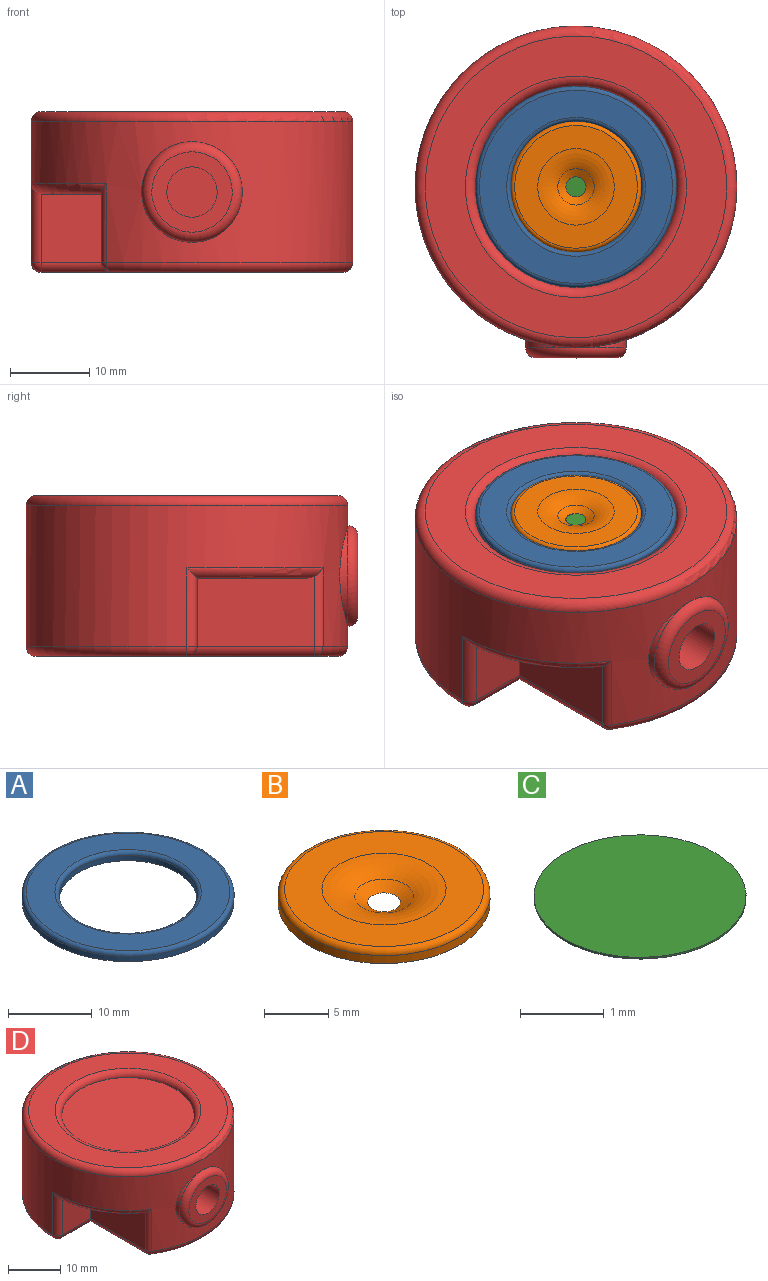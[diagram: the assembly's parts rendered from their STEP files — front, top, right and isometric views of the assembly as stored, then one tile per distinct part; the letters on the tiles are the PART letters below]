
ASSEMBLY  parts=4 mates=3
PART A: 6 faces, bbox 27.5x27.5x1.3 mm
  f0: cylinder r=12.7mm len=25.4mm, axis (0,0,-1), area 60.8mm2, adj f2,f5
  f1: plane 24.38x24.38mm, normal (0,0,1), area 225.7mm2, adj f4,f5
  f2: plane 25.4x25.4mm, normal (0,0,-1), area 292.6mm2, adj f0,f3
  f3: cylinder r=8.26mm len=16.51mm, axis (0,0,1), area 39.5mm2, adj f2,f4
  f4: torus R=8.76mm, axis (0,0,1), area 42.3mm2, adj f1,f3
  f5: torus R=12.19mm, axis (0,0,1), area 62.7mm2, adj f0,f1
PART B: 6 faces, bbox 17.9x17.9x1.3 mm
  f0: cylinder r=8.26mm len=16.51mm, axis (0,0,-1), area 39.5mm2, adj f2,f3
  f1: plane 15.49x15.49mm, normal (0,0,1), area 115.2mm2, adj f3,f5
  f2: plane 16.51x16.51mm, normal (0,0,-1), area 209mm2, adj f0,f4
  f3: torus R=7.75mm, axis (0,0,1), area 40.5mm2, adj f0,f1
  f4: cone r=1.27mm half-angle=60deg, axis (0,0,1), area 13.2mm2, adj f2,f5
  f5: torus R=4.83mm, axis (0,0,1), area 59mm2, adj f1,f4
PART C: 3 faces, bbox 2.5x2.5x0 mm
  f0: cylinder r=1.27mm len=2.54mm, axis (0,0,-1), area 0.2mm2, adj f1,f2
  f1: plane 2.54x2.54mm, normal (0,0,1), area 5.1mm2, adj f0
  f2: plane 2.54x2.54mm, normal (0,0,-1), area 5.1mm2, adj f0
PART D: 23 faces, bbox 44x44x20.3 mm
  f0: cylinder r=6.35mm len=12.7mm, axis (0,1,0), area 10.1mm2, adj f2,f21
  f1: plane 38.1x38.1mm, normal (0,0,-1), area 1039mm2, adj f13,f14,f15
  f2: cylinder r=20.32mm len=40.64mm, axis (0,0,-1), area 1938.7mm2, adj f0,f4,f15,f18,f19,f20,f22
  f3: plane 38.1x38.1mm, normal (0,0,1), area 527mm2, adj f12,f22
  f4: cylinder r=6.35mm len=12.7mm, axis (0,1,0), area 10.1mm2, adj f2,f21
  f5: plane 10.16x10.16mm, normal (0,-1,0), area 49.4mm2, adj f6,f21
  f6: cylinder r=3.17mm len=6.35mm, axis (0,-1,0), area 126.7mm2, adj f5,f7
  f7: plane 6.35x6.35mm, normal (0,-1,0), area 31.7mm2, adj f6
  f8: plane 13.97x7.58mm, normal (0,0,-1), area 71.5mm2, adj f9,f10,f20
  f9: plane 8.64x7.62mm, normal (0,-1,0), area 65.8mm2, adj f8,f10,f14,f19,f20
  f10: plane 14.87x8.88mm, normal (-1,0,0), area 128.3mm2, adj f8,f9,f13,f18,f20
  f11: plane 25.4x25.4mm, normal (0,0,1), area 506.7mm2, adj f12
  f12: torus R=13.97mm, axis (0,0,1), area 165mm2, adj f3,f11
  f13: cylinder r=1.27mm len=16.11mm, axis (0,-1,0), area 30.5mm2, adj f1,f10,f14,f16
  f14: cylinder r=1.27mm len=8.89mm, axis (1,0,0), area 16.1mm2, adj f1,f9,f13,f17
  f15: torus R=19.05mm, axis (0,0,1), area 209mm2, adj f1,f2,f16,f17
  f16: sphere r=1.27mm, area 1.6mm2, adj f13,f15,f18
  f17: sphere r=1.27mm, area 2.5mm2, adj f14,f15,f19
  f18: cylinder r=1.27mm len=9.91mm, axis (0,0,-1), area 12mm2, adj f2,f10,f16,f20
  f19: cylinder r=1.27mm len=9.91mm, axis (0,0,-1), area 18.2mm2, adj f2,f9,f17,f20
  f20: torus R=19.05mm, axis (0,0,-1), area 36.6mm2, adj f2,f8,f9,f10,f18,f19
  f21: torus R=5.08mm, axis (0,-1,0), area 73.8mm2, adj f0,f4,f5
  f22: torus R=19.05mm, axis (0,0,1), area 248.9mm2, adj f2,f3
PLACE A t=(-8.69,0.07,15.57)mm
PLACE B t=(-8.69,0.07,15.57)mm
PLACE C t=(-8.69,0.07,15.57)mm
PLACE D t=(-8.69,0.07,-3.48)mm
MATE fastened C.f0 <-> B.f4  axis (0,0,-1) through (-8.69,0.07,15.57)mm
MATE fastened B.f0 <-> D.f12  axis (0,0,-1) through (-8.69,0.07,15.57)mm
MATE fastened A.f3 <-> D.f12  axis (0,0,-1) through (-8.69,0.07,15.57)mm
